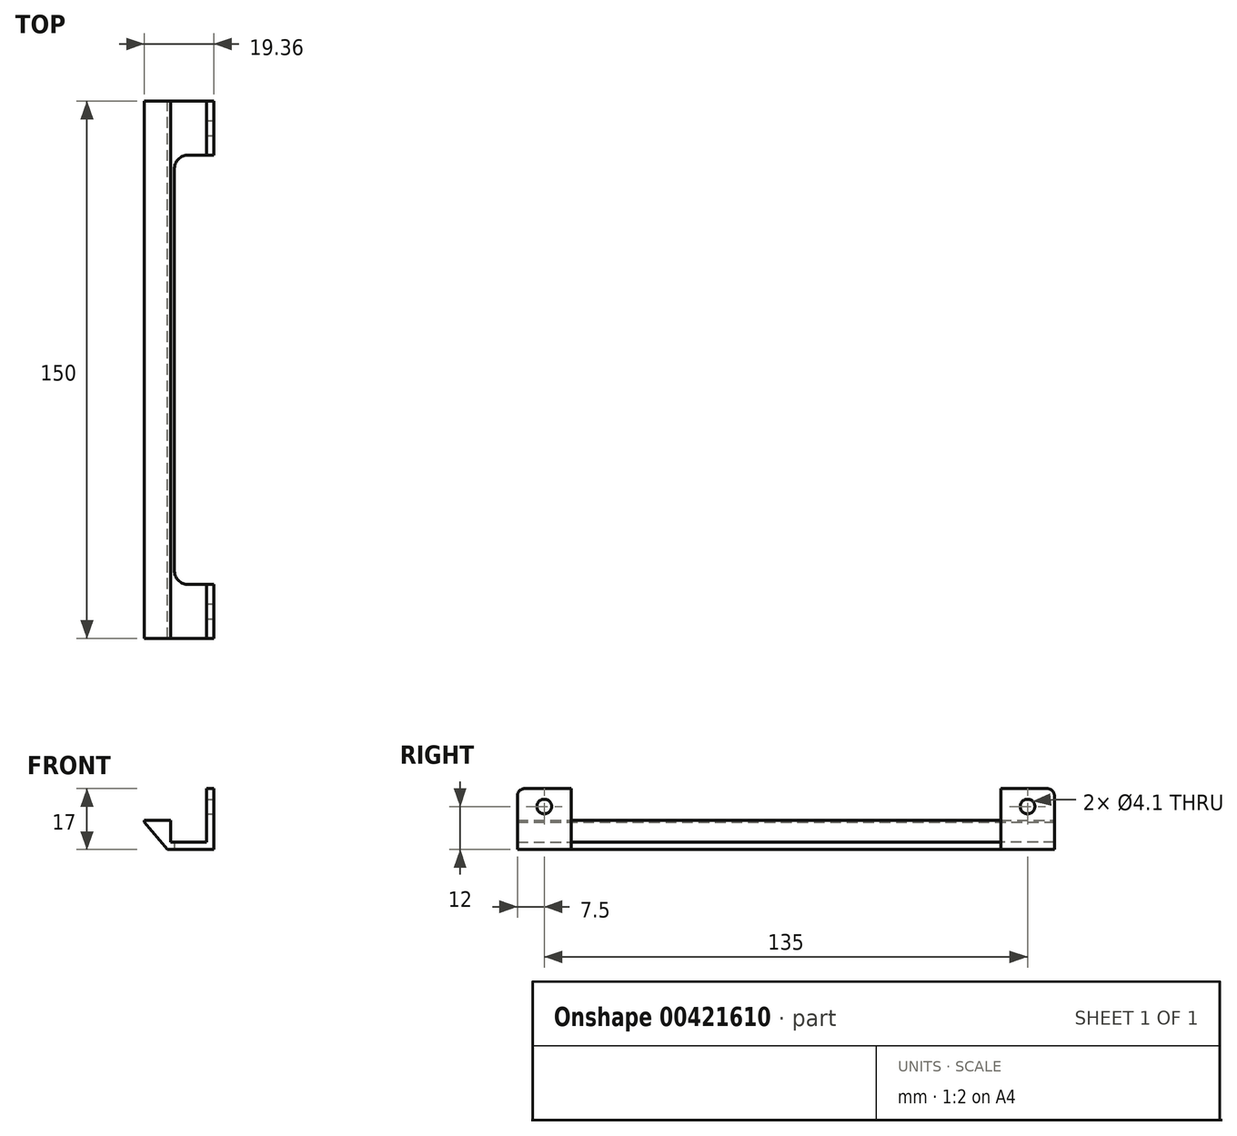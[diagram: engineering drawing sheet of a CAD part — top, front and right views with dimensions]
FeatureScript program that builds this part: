
annotation { "Feature Type Name" : "Feature", "Feature Type Description" : "" }
export const myFeature = defineFeature(function(context is Context, id is Id, definition is map)
    precondition{}
    {
        {
            var Q0;
            Q0=qCreatedBy(makeId("Front.planeOp"),FACE);
            var sketch = newSketch(context, id + "F0", { "sketchPlane" : qUnion([Q0])});
            skLineSegment(sketch, "E0", {"start": v(-12.93, 0) * mm, "end": v(0, 0) * mm});
            skLineSegment(sketch, "E1", {"start": v(0, 0) * mm, "end": v(0, 17) * mm});
            skLineSegment(sketch, "E2", {"start": v(0, 17) * mm, "end": v(-2, 17) * mm});
            skLineSegment(sketch, "E3", {"start": v(-2, 17) * mm, "end": v(-2, 2) * mm});
            skLineSegment(sketch, "E4", {"start": v(-2, 2) * mm, "end": v(-12, 2) * mm});
            skLineSegment(sketch, "E5", {"start": v(-19.36, 7.66) * mm, "end": v(-12.93, 0) * mm});
            skLineSegment(sketch, "E6", {"start": v(-19.36, 7.66) * mm, "end": v(-19.36, 8.16) * mm});
            skLineSegment(sketch, "E7", {"start": v(-19.36, 8.16) * mm, "end": v(-12, 8.16) * mm});
            skLineSegment(sketch, "E8", {"start": v(-12, 8.16) * mm, "end": v(-12, 2) * mm});
            skSolve(sketch);
        }
        {
            var Q0;
            Q0=makeQuery(id+"F0.imprint","IMPRINT",FACE,{"disambiguationData":[TD([[makeQuery(id+"F0.imprint","IMPRINT",EDGE,{"derivedFrom":sQuery(id+"F0.wireOp",EDGE,"E0")}),1.0]])]});
            extrude(context, id + "F1", {"entities" : qUnion([Q0]), "depth" : 75 * mm});
        }
        {
            var Q0;
            Q0=makeQuery(id+"F1.opExtrude","SWEPT_FACE",FACE,{"disambiguationData":[OSD([sQuery(id+"F0.wireOp",EDGE,"E1")])]});
            var sketch = newSketch(context, id + "F2", { "sketchPlane" : qUnion([Q0])});
            skPoint(sketch, "E9", {"position": v(-67.5, 12) * mm});
            skLineSegment(sketch, "E10", {"start": v(-60, 17) * mm, "end": v(-60, 0) * mm});
            skSolve(sketch);
        }
        {
            var Q0;
            Q0=sQuery(id+"F2.wireOp",VERTEX,"E9");
            var Q1;
            Q1=makeQuery(id+"F1.opExtrude","SWEPT_BODY",BODY,{"disambiguationData":[OSD([sQuery(id+"F0.wireOp",EDGE,"E0"),sQuery(id+"F0.wireOp",EDGE,"E1"),sQuery(id+"F0.wireOp",EDGE,"E2"),sQuery(id+"F0.wireOp",EDGE,"E3"),sQuery(id+"F0.wireOp",EDGE,"E4"),sQuery(id+"F0.wireOp",EDGE,"mUH326NZ-KSFU-6OOB-ISw1-4K6WY4FAWbn8"),sQuery(id+"F0.wireOp",EDGE,"E5"),sQuery(id+"F0.wireOp",EDGE,"E6"),sQuery(id+"F0.wireOp",EDGE,"E7"),sQuery(id+"F0.wireOp",EDGE,"E8")])]});
            hole(context, id + "F3", {"style" : HoleStyle.SIMPLE, "endStyle" : HoleEndStyle.THROUGH, "holeDiameter" : 4.1 * mm, "isTappedThrough" : true, "tappedDepth" : 12 * mm, "tapClearance" : 3, "locations" : qUnion([Q0]), "scope" : qUnion([Q1])});
        }
        {
            var Q0;
            {var subQ0=sQuery(id+"F2.wireOp",EDGE,"E10");Q0=makeQuery(id+"F2.imprint","IMPRINT",FACE,{"disambiguationData":[TD([[makeQuery(id+"F2.imprint","IMPRINT",EDGE,{"derivedFrom":subQ0}),1.0]])]});}
            var Q1;
            Q1=makeQuery(id+"F1.opExtrude","SWEPT_FACE",FACE,{"disambiguationData":[OSD([sQuery(id+"F0.wireOp",EDGE,"E8")])]});
            extrude(context, id + "F4", {"entities" : qUnion([Q0]), "operationType" : NewBodyOperationType.REMOVE, "oppositeDirection" : true, "endBoundEntityFace" : qUnion([Q1]), "depth" : 11 * mm});
        }
        {
            var Q0;
            Q0=makeQuery(id+"F4.boolean.opBoolean","COPY",EDGE,{"derivedFrom":makeQuery(id+"F4.opExtrude","CAP_EDGE",EDGE,{"disambiguationData":[OSD([sQuery(id+"F2.wireOp",EDGE,"E10")])],"isStart":false})});
            fillet(context, id + "F5", {"entities" : qUnion([Q0]), "radius" : 4 * mm, "tangentPropagation" : true, "allowEdgeOverflow" : false});
        }
        {
            var Q0;
            Q0=makeQuery(id+"F4.boolean.opBoolean","COPY",EDGE,{"derivedFrom":makeQuery(id+"F4.opExtrude","SWEPT_EDGE",EDGE,{"disambiguationData":[OSD([sQuery(id+"F0.wireOp",EDGE,"E1"),sQuery(id+"F0.wireOp",EDGE,"E2"),sQuery(id+"F2.wireOp",EDGE,"E10")])]})});
            var Q1;
            Q1=makeQuery(id+"F1.opExtrude","CAP_EDGE",EDGE,{"disambiguationData":[OSD([sQuery(id+"F0.wireOp",EDGE,"E2")])],"isStart":false});
            fillet(context, id + "F6", {"entities" : qUnion([Q0, Q1]), "radius" : 2 * mm, "tangentPropagation" : true, "allowEdgeOverflow" : false});
        }
        {
            var Q0;
            Q0=makeQuery(id+"F1.opExtrude","SWEPT_BODY",BODY,{"disambiguationData":[OSD([sQuery(id+"F0.wireOp",EDGE,"E0"),sQuery(id+"F0.wireOp",EDGE,"E1"),sQuery(id+"F0.wireOp",EDGE,"E2"),sQuery(id+"F0.wireOp",EDGE,"E3"),sQuery(id+"F0.wireOp",EDGE,"E4"),sQuery(id+"F0.wireOp",EDGE,"E5"),sQuery(id+"F0.wireOp",EDGE,"E6"),sQuery(id+"F0.wireOp",EDGE,"E7"),sQuery(id+"F0.wireOp",EDGE,"E8")])]});
            var Q1;
            Q1=makeQuery(id+"F1.opExtrude","CAP_FACE",FACE,{"disambiguationData":[OSD([sQuery(id+"F0.wireOp",EDGE,"E0"),sQuery(id+"F0.wireOp",EDGE,"E1"),sQuery(id+"F0.wireOp",EDGE,"E2"),sQuery(id+"F0.wireOp",EDGE,"E3"),sQuery(id+"F0.wireOp",EDGE,"E4"),sQuery(id+"F0.wireOp",EDGE,"E5"),sQuery(id+"F0.wireOp",EDGE,"E6"),sQuery(id+"F0.wireOp",EDGE,"E7"),sQuery(id+"F0.wireOp",EDGE,"E8")])],"isStart":true});
            mirror(context, id + "F7", {"operationType" : NewBodyOperationType.ADD, "entities" : qUnion([Q0]), "mirrorPlane" : qUnion([Q1])});
        }
    });
